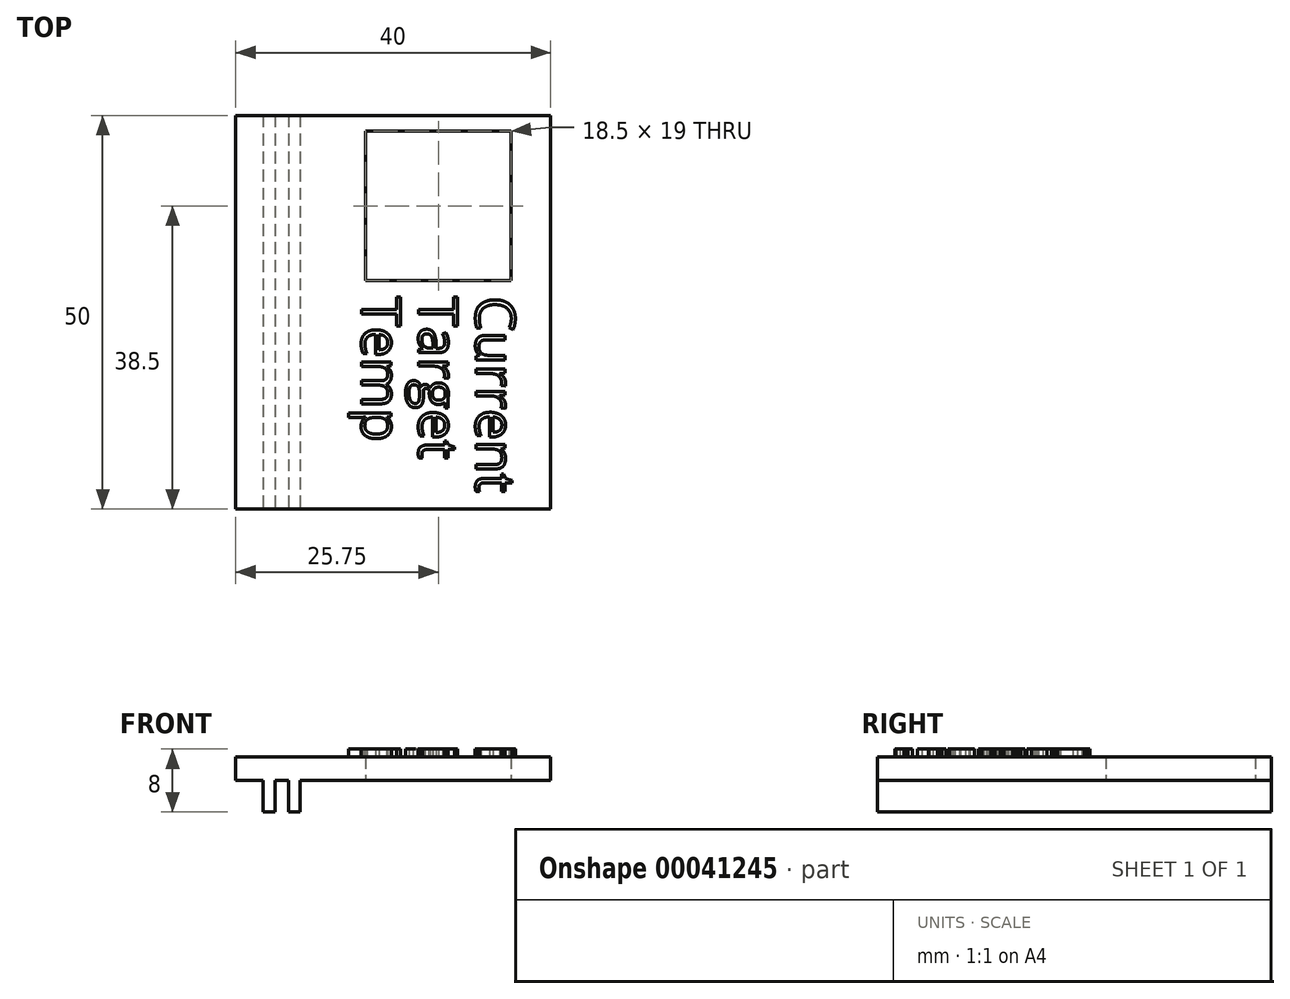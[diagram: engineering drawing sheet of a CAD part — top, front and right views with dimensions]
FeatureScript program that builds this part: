
annotation { "Feature Type Name" : "Feature", "Feature Type Description" : "" }
export const myFeature = defineFeature(function(context is Context, id is Id, definition is map)
    precondition{}
    {
        {
            var Q0;
            Q0=qCreatedBy(makeId("Top.planeOp"),FACE);
            var sketch = newSketch(context, id + "F0", { "sketchPlane" : qUnion([Q0])});
            skLineSegment(sketch, "E0.rect.bottom", {"start": v(20, 25) * mm, "end": v(-20, 25) * mm});
            skLineSegment(sketch, "E0.rect.top", {"start": v(20, -25) * mm, "end": v(-20, -25) * mm});
            skLineSegment(sketch, "E0.rect.left", {"start": v(20, 25) * mm, "end": v(20, -25) * mm});
            skLineSegment(sketch, "E0.rect.right", {"start": v(-20, 25) * mm, "end": v(-20, -25) * mm});
            skPoint(sketch, "E0.rect.middle", {"position": v(0, 0) * mm});
            skLineSegment(sketch, "E1.bottom", {"start": v(-15, 25) * mm, "end": v(-13.3, 25) * mm});
            skLineSegment(sketch, "E1.top", {"start": v(-15, -25) * mm, "end": v(-13.3, -25) * mm});
            skLineSegment(sketch, "E1.left", {"start": v(-15, 25) * mm, "end": v(-15, -25) * mm});
            skLineSegment(sketch, "E1.right", {"start": v(-13.3, 25) * mm, "end": v(-13.3, -25) * mm});
            skLineSegment(sketch, "E2.bottom", {"start": v(15, 23) * mm, "end": v(-3.5, 23) * mm});
            skLineSegment(sketch, "E2.top", {"start": v(15, 4) * mm, "end": v(-3.5, 4) * mm});
            skLineSegment(sketch, "E2.left", {"start": v(15, 23) * mm, "end": v(15, 4) * mm});
            skLineSegment(sketch, "E2.right", {"start": v(-3.5, 23) * mm, "end": v(-3.5, 4) * mm});
            skLineSegment(sketch, "E3", {"start": v(-16.5, 25) * mm, "end": v(-16.5, -25) * mm});
            skLineSegment(sketch, "E4", {"start": v(-11.8, 25) * mm, "end": v(-11.8, -25) * mm});
            skLineSegment(sketch, "E5", {"start": v(-13.3, 22.5) * mm, "end": v(-15, 22.5) * mm});
            skLineSegment(sketch, "E6", {"start": v(-15, -22.5) * mm, "end": v(-13.3, -22.5) * mm});
            skSolve(sketch);
        }
        {
            var Q0;
            {var subQ2=sQuery(id+"F0.wireOp",EDGE,"E0.rect.left");Q0=makeQuery(id+"F0.imprint","IMPRINT",FACE,{"disambiguationData":[TD([[makeQuery(id+"F0.imprint","IMPRINT",EDGE,{"derivedFrom":subQ2}),-1.0]])]});}
            var Q1;
            Q1 = qSketchRegion(id + "F0", true);
            var Q2;
            Q2=makeQuery(id+"F0.imprint","IMPRINT",FACE,{"disambiguationData":[TD([[makeQuery(id+"F0.imprint","IMPRINT",EDGE,{"derivedFrom":sQuery(id+"F0.wireOp",EDGE,"d8fcf707-4972-4969-a602-c9377c3f4dec.sketch_text.stroke-190")}),1.0]])]});
            var Q3;
            Q3=makeQuery(id+"F0.imprint","IMPRINT",FACE,{"disambiguationData":[TD([[makeQuery(id+"F0.imprint","IMPRINT",EDGE,{"derivedFrom":sQuery(id+"F0.wireOp",EDGE,"d8fcf707-4972-4969-a602-c9377c3f4dec.sketch_text.stroke-140")}),1.0]])]});
            var Q4;
            Q4=makeQuery(id+"F0.imprint","IMPRINT",FACE,{"disambiguationData":[TD([[makeQuery(id+"F0.imprint","IMPRINT",EDGE,{"derivedFrom":sQuery(id+"F0.wireOp",EDGE,"d8fcf707-4972-4969-a602-c9377c3f4dec.sketch_text.stroke-298")}),-1.0]])]});
            var Q5;
            Q5=makeQuery(id+"F0.imprint","IMPRINT",FACE,{"disambiguationData":[TD([[makeQuery(id+"F0.imprint","IMPRINT",EDGE,{"derivedFrom":sQuery(id+"F0.wireOp",EDGE,"d8fcf707-4972-4969-a602-c9377c3f4dec.sketch_text.stroke-265")}),1.0]])]});
            var Q6;
            Q6=makeQuery(id+"F0.imprint","IMPRINT",FACE,{"disambiguationData":[TD([[makeQuery(id+"F0.imprint","IMPRINT",EDGE,{"derivedFrom":sQuery(id+"F0.wireOp",EDGE,"d8fcf707-4972-4969-a602-c9377c3f4dec.sketch_text.stroke-270")}),-1.0]])]});
            var Q7;
            Q7=makeQuery(id+"F0.imprint","IMPRINT",FACE,{"disambiguationData":[TD([[makeQuery(id+"F0.imprint","IMPRINT",EDGE,{"derivedFrom":sQuery(id+"F0.wireOp",EDGE,"d8fcf707-4972-4969-a602-c9377c3f4dec.sketch_text.stroke-314")}),1.0]])]});
            var Q8;
            Q8=makeQuery(id+"F0.imprint","IMPRINT",FACE,{"disambiguationData":[TD([[makeQuery(id+"F0.imprint","IMPRINT",EDGE,{"derivedFrom":sQuery(id+"F0.wireOp",EDGE,"E1.bottom")}),-1.0]])]});
            var Q9;
            Q9=makeQuery(id+"F0.imprint","IMPRINT",FACE,{"disambiguationData":[TD([[makeQuery(id+"F0.imprint","IMPRINT",EDGE,{"derivedFrom":sQuery(id+"F0.wireOp",EDGE,"d8fcf707-4972-4969-a602-c9377c3f4dec.sketch_text.stroke-58")}),-1.0]])]});
            var Q10;
            Q10=makeQuery(id+"F0.imprint","IMPRINT",FACE,{"disambiguationData":[TD([[makeQuery(id+"F0.imprint","IMPRINT",EDGE,{"derivedFrom":sQuery(id+"F0.wireOp",EDGE,"d8fcf707-4972-4969-a602-c9377c3f4dec.sketch_text.stroke-219")}),1.0]])]});
            var Q11;
            {var subQ1=sQuery(id+"F0.wireOp",EDGE,"E0.rect.right");Q11=makeQuery(id+"F0.imprint","IMPRINT",FACE,{"disambiguationData":[TD([[makeQuery(id+"F0.imprint","IMPRINT",EDGE,{"derivedFrom":subQ1}),1.0]])]});}
            var Q12;
            Q12=makeQuery(id+"F0.imprint","IMPRINT",FACE,{"disambiguationData":[TD([[makeQuery(id+"F0.imprint","IMPRINT",EDGE,{"derivedFrom":sQuery(id+"F0.wireOp",EDGE,"d8fcf707-4972-4969-a602-c9377c3f4dec.sketch_text.stroke-72")}),1.0]])]});
            var Q13;
            Q13=makeQuery(id+"F0.imprint","IMPRINT",FACE,{"disambiguationData":[TD([[makeQuery(id+"F0.imprint","IMPRINT",EDGE,{"derivedFrom":sQuery(id+"F0.wireOp",EDGE,"d8fcf707-4972-4969-a602-c9377c3f4dec.sketch_text.stroke-199")}),1.0]])]});
            var Q14;
            Q14=makeQuery(id+"F0.imprint","IMPRINT",FACE,{"disambiguationData":[TD([[makeQuery(id+"F0.imprint","IMPRINT",EDGE,{"derivedFrom":sQuery(id+"F0.wireOp",EDGE,"d8fcf707-4972-4969-a602-c9377c3f4dec.sketch_text.stroke-94")}),-1.0]])]});
            var Q15;
            Q15=makeQuery(id+"F0.imprint","IMPRINT",FACE,{"disambiguationData":[TD([[makeQuery(id+"F0.imprint","IMPRINT",EDGE,{"derivedFrom":sQuery(id+"F0.wireOp",EDGE,"d8fcf707-4972-4969-a602-c9377c3f4dec.sketch_text.stroke-148")}),-1.0]])]});
            var Q16;
            Q16=makeQuery(id+"F0.imprint","IMPRINT",FACE,{"disambiguationData":[TD([[makeQuery(id+"F0.imprint","IMPRINT",EDGE,{"derivedFrom":sQuery(id+"F0.wireOp",EDGE,"d8fcf707-4972-4969-a602-c9377c3f4dec.sketch_text.stroke-113")}),-1.0]])]});
            var Q17;
            Q17=makeQuery(id+"F0.imprint","IMPRINT",FACE,{"disambiguationData":[TD([[makeQuery(id+"F0.imprint","IMPRINT",EDGE,{"derivedFrom":sQuery(id+"F0.wireOp",EDGE,"d8fcf707-4972-4969-a602-c9377c3f4dec.sketch_text.stroke-161")}),-1.0]])]});
            var Q18;
            Q18=makeQuery(id+"F0.imprint","IMPRINT",FACE,{"disambiguationData":[TD([[makeQuery(id+"F0.imprint","IMPRINT",EDGE,{"derivedFrom":sQuery(id+"F0.wireOp",EDGE,"d8fcf707-4972-4969-a602-c9377c3f4dec.sketch_text.stroke-251")}),-1.0]])]});
            var Q19;
            Q19=makeQuery(id+"F0.imprint","IMPRINT",FACE,{"disambiguationData":[TD([[makeQuery(id+"F0.imprint","IMPRINT",EDGE,{"derivedFrom":sQuery(id+"F0.wireOp",EDGE,"d8fcf707-4972-4969-a602-c9377c3f4dec.sketch_text.stroke-205")}),-1.0]])]});
            var Q20;
            Q20=makeQuery(id+"F0.imprint","IMPRINT",FACE,{"disambiguationData":[TD([[makeQuery(id+"F0.imprint","IMPRINT",EDGE,{"derivedFrom":sQuery(id+"F0.wireOp",EDGE,"d8fcf707-4972-4969-a602-c9377c3f4dec.sketch_text.stroke-121")}),-1.0]])]});
            var Q21;
            Q21=makeQuery(id+"F0.imprint","IMPRINT",FACE,{"disambiguationData":[TD([[makeQuery(id+"F0.imprint","IMPRINT",EDGE,{"derivedFrom":sQuery(id+"F0.wireOp",EDGE,"d8fcf707-4972-4969-a602-c9377c3f4dec.sketch_text.stroke-243")}),-1.0]])]});
            var Q22;
            Q22=makeQuery(id+"F0.imprint","IMPRINT",FACE,{"disambiguationData":[TD([[makeQuery(id+"F0.imprint","IMPRINT",EDGE,{"derivedFrom":sQuery(id+"F0.wireOp",EDGE,"d8fcf707-4972-4969-a602-c9377c3f4dec.sketch_text.stroke-224")}),-1.0]])]});
            var Q23;
            Q23=makeQuery(id+"F0.imprint","IMPRINT",FACE,{"disambiguationData":[TD([[makeQuery(id+"F0.imprint","IMPRINT",EDGE,{"derivedFrom":sQuery(id+"F0.wireOp",EDGE,"d8fcf707-4972-4969-a602-c9377c3f4dec.sketch_text.stroke-0")}),-1.0]])]});
            var Q24;
            Q24=makeQuery(id+"F0.imprint","IMPRINT",FACE,{"disambiguationData":[TD([[makeQuery(id+"F0.imprint","IMPRINT",EDGE,{"derivedFrom":sQuery(id+"F0.wireOp",EDGE,"d8fcf707-4972-4969-a602-c9377c3f4dec.sketch_text.stroke-15")}),-1.0]])]});
            var Q25;
            Q25=makeQuery(id+"F0.imprint","IMPRINT",FACE,{"disambiguationData":[TD([[makeQuery(id+"F0.imprint","IMPRINT",EDGE,{"derivedFrom":sQuery(id+"F0.wireOp",EDGE,"d8fcf707-4972-4969-a602-c9377c3f4dec.sketch_text.stroke-32")}),-1.0]])]});
            var Q26;
            Q26=makeQuery(id+"F0.imprint","IMPRINT",FACE,{"disambiguationData":[TD([[makeQuery(id+"F0.imprint","IMPRINT",EDGE,{"derivedFrom":sQuery(id+"F0.wireOp",EDGE,"d8fcf707-4972-4969-a602-c9377c3f4dec.sketch_text.stroke-45")}),-1.0]])]});
            var Q27;
            Q27=makeQuery(id+"F0.imprint","IMPRINT",FACE,{"disambiguationData":[TD([[makeQuery(id+"F0.imprint","IMPRINT",EDGE,{"derivedFrom":sQuery(id+"F0.wireOp",EDGE,"d8fcf707-4972-4969-a602-c9377c3f4dec.sketch_text.stroke-77")}),-1.0]])]});
            var Q28;
            {var subQ1=sQuery(id+"F0.wireOp",EDGE,"E5");Q28=makeQuery(id+"F0.imprint","IMPRINT",FACE,{"disambiguationData":[TD([[makeQuery(id+"F0.imprint","IMPRINT",EDGE,{"derivedFrom":subQ1}),1.0]])]});}
            extrude(context, id + "F1", {"entities" : qUnion([Q0, Q1, Q2, Q3, Q4, Q5, Q6, Q7, Q8, Q9, Q10, Q11, Q12, Q13, Q14, Q15, Q16, Q17, Q18, Q19, Q20, Q21, Q22, Q23, Q24, Q25, Q26, Q27, Q28]), "depth" : 3 * mm});
        }
        {
            var Q0;
            {var subQ1=sQuery(id+"F0.wireOp",EDGE,"E1.right");Q0=makeQuery(id+"F0.imprint","IMPRINT",FACE,{"disambiguationData":[TD([[makeQuery(id+"F0.imprint","IMPRINT",EDGE,{"derivedFrom":subQ1}),1.0]])]});}
            var Q1;
            {var subQ1=sQuery(id+"F0.wireOp",EDGE,"E1.left");Q1=makeQuery(id+"F0.imprint","IMPRINT",FACE,{"disambiguationData":[TD([[makeQuery(id+"F0.imprint","IMPRINT",EDGE,{"derivedFrom":subQ1}),-1.0]])]});}
            var Q2;
            {var subQ3=sQuery(id+"F0.wireOp",EDGE,"E1.bottom");Q2=makeQuery(id+"F0.imprint","IMPRINT",FACE,{"disambiguationData":[TD([[makeQuery(id+"F0.imprint","IMPRINT",EDGE,{"derivedFrom":subQ3}),-1.0]])]});}
            var Q3;
            {var subQ3=sQuery(id+"F0.wireOp",EDGE,"E1.top");Q3=makeQuery(id+"F0.imprint","IMPRINT",FACE,{"disambiguationData":[TD([[makeQuery(id+"F0.imprint","IMPRINT",EDGE,{"derivedFrom":subQ3}),1.0]])]});}
            extrude(context, id + "F2", {"entities" : qUnion([Q0, Q1, Q2, Q3]), "operationType" : NewBodyOperationType.ADD, "oppositeDirection" : true, "depth" : 4 * mm});
        }
        {
            var Q0;
            {var subQ0=sQuery(id+"F0.wireOp",EDGE,"E0.rect.bottom");var subQ1=sQuery(id+"F0.wireOp",EDGE,"E0.rect.top");var subQ2=sQuery(id+"F0.wireOp",EDGE,"E0.rect.left");var subQ3=sQuery(id+"F0.wireOp",EDGE,"E1.bottom");var subQ4=sQuery(id+"F0.wireOp",EDGE,"E1.top");var subQ5=sQuery(id+"F0.wireOp",EDGE,"E2.bottom");var subQ6=sQuery(id+"F0.wireOp",EDGE,"E2.top");var subQ7=sQuery(id+"F0.wireOp",EDGE,"E2.left");var subQ8=sQuery(id+"F0.wireOp",EDGE,"E2.right");Q0=makeQuery(id+"F2.boolean.opBoolean","SPLIT",FACE,{"disambiguationData":[TD([makeQuery(id+"F1.opExtrude","SWEPT_FACE",FACE,{"disambiguationData":[OSD([subQ2])]})])],"derivedFrom":makeQuery(id+"F1.opExtrude","CAP_FACE",FACE,{"disambiguationData":[OSD([subQ0,subQ1,subQ2,sQuery(id+"F0.wireOp",EDGE,"E0.rect.right"),subQ3,subQ4,subQ5,subQ6,subQ7,subQ8])],"isStart":false})});}
            var sketch = newSketch(context, id + "F3", { "sketchPlane" : qUnion([Q0])});
            skText(sketch, "E7", { "text": "Current", "fontName": "OpenSans-Regular.ttf"});
            skText(sketch, "E8", { "text": "Target", "fontName": "OpenSans-Regular.ttf"});
            skText(sketch, "E9", { "text": "Temp", "fontName": "OpenSans-Regular.ttf"});
            const initialGuessF3  = {"E7": [0.0105, 0.002, 0, -1, 0.005], "E8": [0.00325, 0.002, 0, -1, 0.005], "E9": [-0.004, 0.002, 0, -1, 0.005]};
            skSetInitialGuess(sketch, initialGuessF3);
            skSolve(sketch);
        }
        {
            var Q0;
            Q0 = qSketchRegion(id + "F3", true);
            extrude(context, id + "F4", {"entities" : qUnion([Q0]), "operationType" : NewBodyOperationType.ADD, "depth" : 1 * mm});
        }
    });
